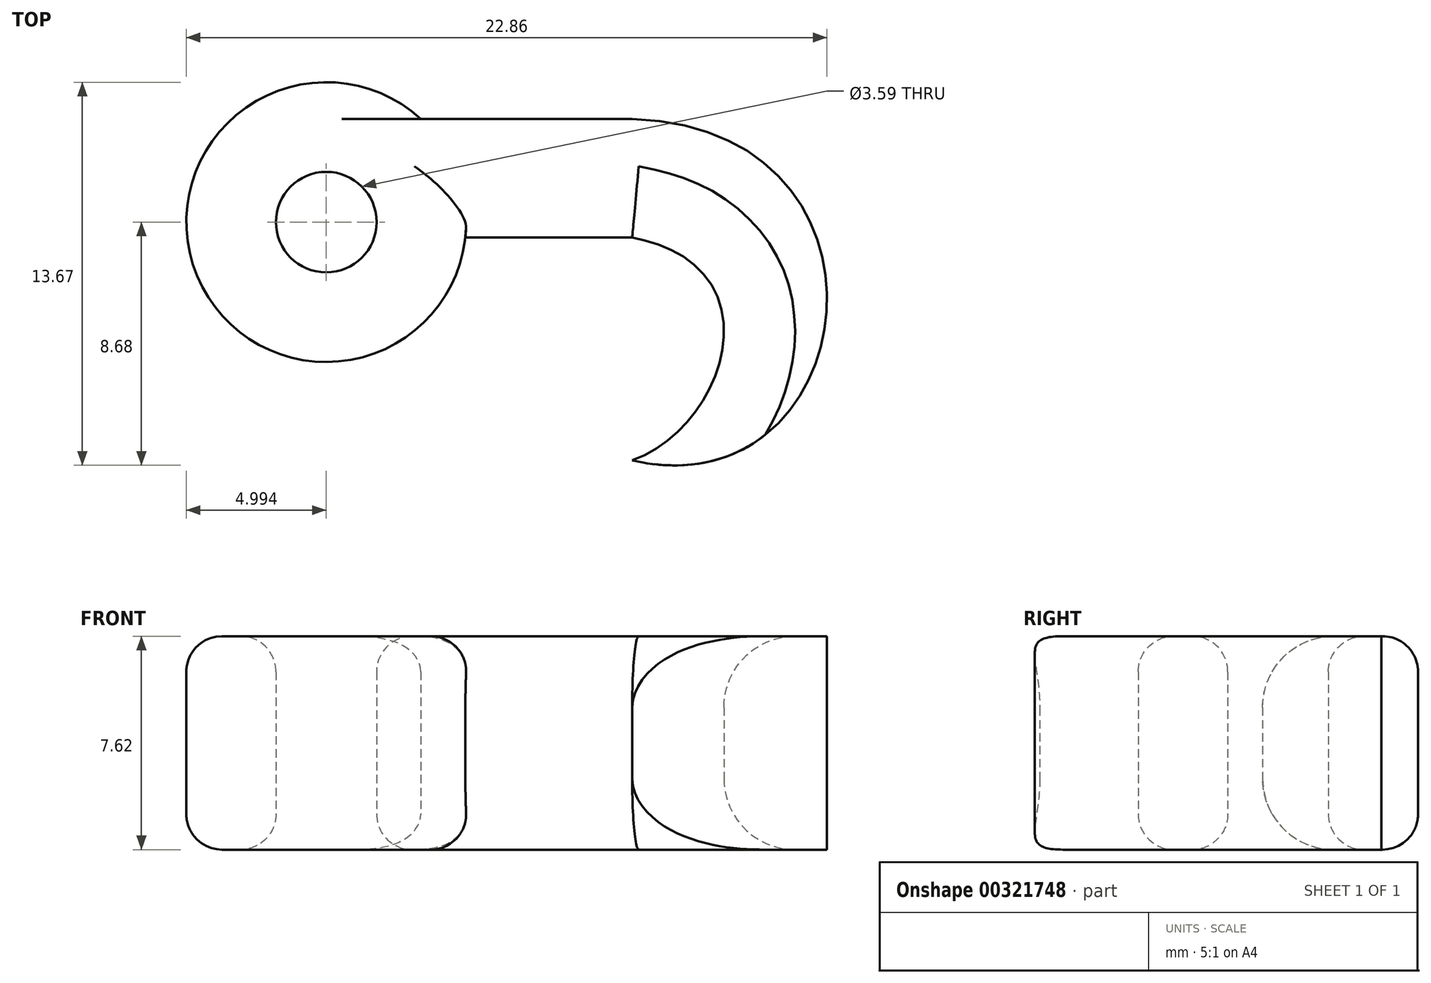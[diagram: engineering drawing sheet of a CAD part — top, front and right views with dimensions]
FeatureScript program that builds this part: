
annotation { "Feature Type Name" : "Feature", "Feature Type Description" : "" }
export const myFeature = defineFeature(function(context is Context, id is Id, definition is map)
    precondition{}
    {
        {
            var Q0;
            Q0=qCreatedBy(makeId("Top.planeOp"),FACE);
            var sketch = newSketch(context, id + "F0", { "sketchPlane" : qUnion([Q0])});
            skLineSegment(sketch, "E0.bottom", {"start": v(-12.7, 5.93) * mm, "end": v(12.7, 5.93) * mm, "construction": true});
            skLineSegment(sketch, "E0.top", {"start": v(-12.7, -5.93) * mm, "end": v(12.7, -5.93) * mm, "construction": true});
            skLineSegment(sketch, "E0.left", {"start": v(-12.7, 5.93) * mm, "end": v(-12.7, -5.93) * mm, "construction": true});
            skLineSegment(sketch, "E0.right", {"start": v(12.7, 5.93) * mm, "end": v(12.7, -5.93) * mm, "construction": true});
            skPoint(sketch, "E0.middle", {"position": v(0, 0) * mm});
            skCircle(sketch, "E1", {"center": v(-6.44, 0) * mm, "radius": 5 * mm});
            skCircle(sketch, "E2", {"center": v(-6.44, 0) * mm, "radius": 1.8 * mm});
            skLineSegment(sketch, "E3", {"start": v(-3.06, 3.68) * mm, "end": v(4.48, 3.68) * mm});
            skLineSegment(sketch, "E4", {"start": v(4.48, 3.68) * mm, "end": v(4.48, -0.55) * mm});
            skLineSegment(sketch, "E5", {"start": v(4.48, -0.55) * mm, "end": v(-1.47, -0.55) * mm});
            skFitSpline(sketch, "E6", {"points": [v(4.48, -0.55) * mm, v(4.48, -8.5) * mm], "startDerivative": vector(15.88, -2.96) * mm, "endDerivative": vector(-10, -3.53) * mm});
            skFitSpline(sketch, "E7", {"points": [v(4.48, 3.68) * mm, v(4.48, -8.5) * mm], "startDerivative": vector(30.64, -1) * mm, "endDerivative": vector(-24.79, 5.7) * mm});
            skSolve(sketch);
        }
        {
            var Q0;
            {var subQ0=sQuery(id+"F0.wireOp",EDGE,"E3");Q0=makeQuery(id+"F0.imprint","IMPRINT",FACE,{"disambiguationData":[TD([[makeQuery(id+"F0.imprint","IMPRINT",EDGE,{"derivedFrom":subQ0}),-1.0]])]});}
            var Q1;
            Q1=makeQuery(id+"F0.imprint","IMPRINT",FACE,{"disambiguationData":[TD([[makeQuery(id+"F0.imprint","IMPRINT",EDGE,{"derivedFrom":sQuery(id+"F0.wireOp",EDGE,"E4")}),1.0]])]});
            var Q2;
            Q2=makeQuery(id+"F0.imprint","IMPRINT",FACE,{"disambiguationData":[TD([[makeQuery(id+"F0.imprint","IMPRINT",EDGE,{"derivedFrom":sQuery(id+"F0.wireOp",EDGE,"E2")}),-1.0]])]});
            extrude(context, id + "F1", {"entities" : qUnion([Q0, Q1, Q2]), "depth" : 7.62 * mm});
        }
        {
            var Q0;
            Q0=makeQuery(id+"F1.opExtrude","CAP_EDGE",EDGE,{"disambiguationData":[OSD([sQuery(id+"F0.wireOp",EDGE,"E5")])],"isStart":false});
            var Q1;
            Q1=makeQuery(id+"F1.opExtrude","CAP_EDGE",EDGE,{"disambiguationData":[OSD([sQuery(id+"F0.wireOp",EDGE,"E6")])],"isStart":false});
            var Q2;
            Q2=makeQuery(id+"F1.opExtrude","CAP_EDGE",EDGE,{"disambiguationData":[OSD([sQuery(id+"F0.wireOp",EDGE,"E5")])],"isStart":true});
            var Q3;
            Q3=makeQuery(id+"F1.opExtrude","CAP_EDGE",EDGE,{"disambiguationData":[OSD([sQuery(id+"F0.wireOp",EDGE,"E6")])],"isStart":true});
            fillet(context, id + "F2", {"entities" : qUnion([Q0, Q1, Q2, Q3]), "radius" : 2.54 * mm, "tangentPropagation" : true, "allowEdgeOverflow" : false});
        }
        {
            var Q0;
            Q0=makeQuery(id+"F1.opExtrude","CAP_EDGE",EDGE,{"disambiguationData":[OSD([sQuery(id+"F0.wireOp",EDGE,"E1")])],"isStart":false});
            var Q1;
            Q1=makeQuery(id+"F1.opExtrude","CAP_EDGE",EDGE,{"disambiguationData":[OSD([sQuery(id+"F0.wireOp",EDGE,"E1")])],"isStart":true});
            var Q2;
            Q2=makeQuery(id+"F1.opExtrude","CAP_EDGE",EDGE,{"disambiguationData":[OSD([sQuery(id+"F0.wireOp",EDGE,"E2")])],"isStart":true});
            var Q3;
            Q3=makeQuery(id+"F1.opExtrude","CAP_EDGE",EDGE,{"disambiguationData":[OSD([sQuery(id+"F0.wireOp",EDGE,"E2")])],"isStart":false});
            fillet(context, id + "F3", {"entities" : qUnion([Q0, Q1, Q2, Q3]), "radius" : 1.27 * mm, "tangentPropagation" : true, "allowEdgeOverflow" : false});
        }
    });
